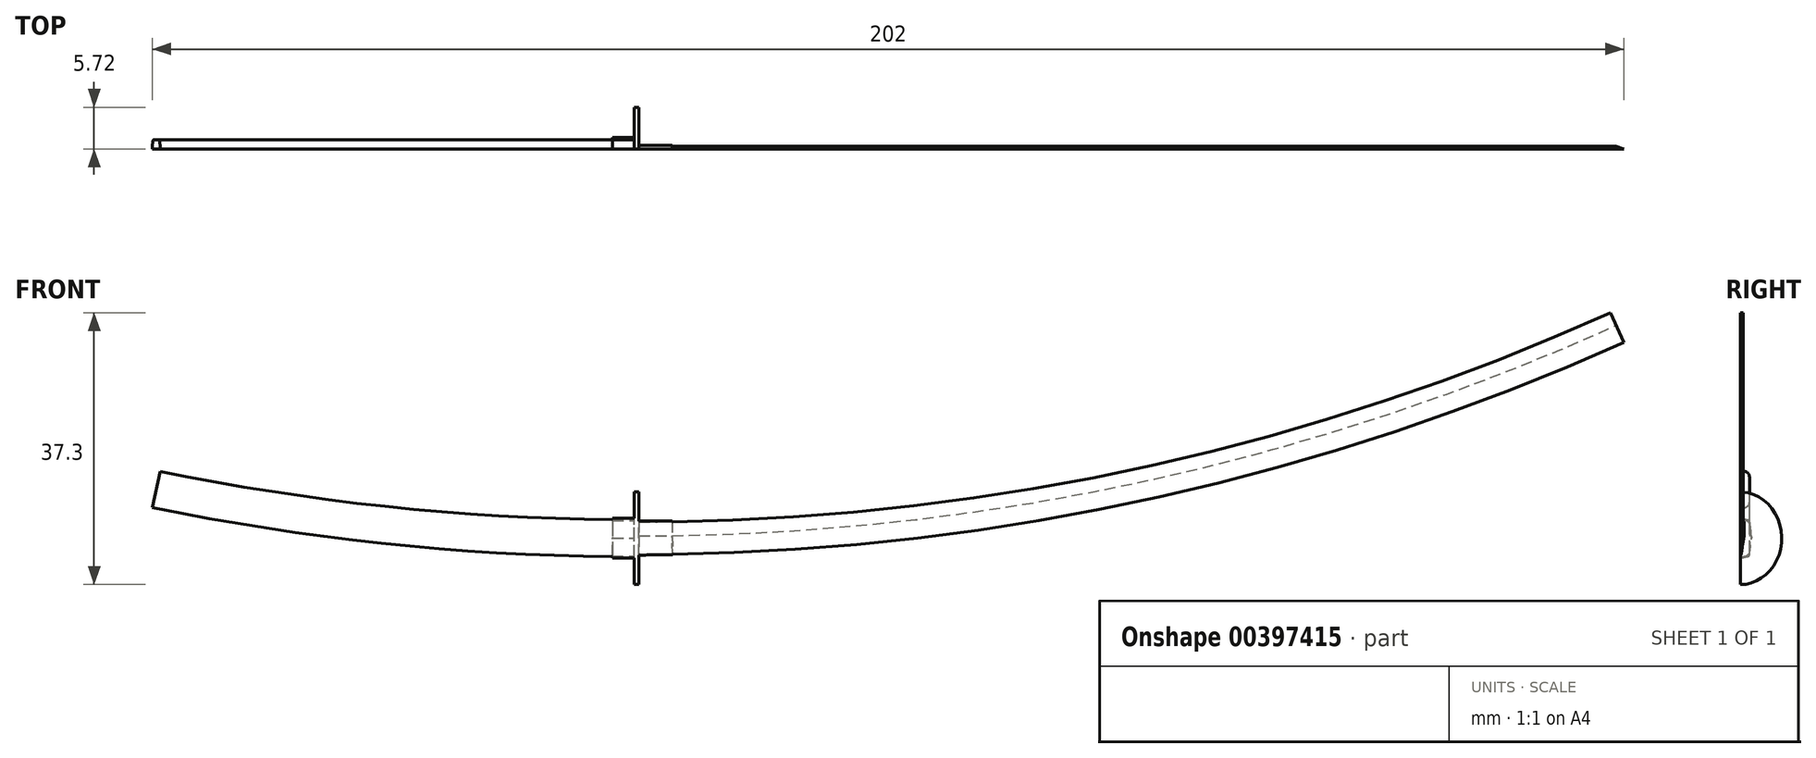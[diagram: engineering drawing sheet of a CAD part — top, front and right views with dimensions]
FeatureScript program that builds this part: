
annotation { "Feature Type Name" : "Feature", "Feature Type Description" : "" }
export const myFeature = defineFeature(function(context is Context, id is Id, definition is map)
    precondition{}
    {
        {
            var Q0;
            Q0=qCreatedBy(makeId("Front.planeOp"),FACE);
            var sketch = newSketch(context, id + "F0", { "sketchPlane" : qUnion([Q0])});
            skArc(sketch, "E0", {"start": v(0, 0) * mm, "mid": v(68.78, 7.3) * mm, "end": v(134.49, 28.9) * mm});
            skArc(sketch, "E1", {"start": v(0, 0) * mm, "mid": v(-33.12, 1.68) * mm, "end": v(-65.9, 6.7) * mm});
            skSolve(sketch);
        }
        {
            var Q0;
            Q0=qCreatedBy(makeId("Right.planeOp"),FACE);
            var sketch = newSketch(context, id + "F1", { "sketchPlane" : qUnion([Q0])});
            skLineSegment(sketch, "E2", {"start": v(0, 0) * mm, "end": v(0, 1.9) * mm});
            skLineSegment(sketch, "E3", {"start": v(0, 1.9) * mm, "end": v(0.38, 1.9) * mm});
            skLineSegment(sketch, "E4", {"start": v(0.38, 1.9) * mm, "end": v(0.38, 0) * mm});
            skLineSegment(sketch, "E5", {"start": v(0, 0) * mm, "end": v(0, -2.54) * mm});
            skLineSegment(sketch, "E6", {"start": v(0, -2.54) * mm, "end": v(0.38, 0) * mm});
            skSolve(sketch);
        }
        {
            var Q0;
            Q0=makeQuery(id+"F1.imprint","IMPRINT",FACE,{"disambiguationData":[TD([[makeQuery(id+"F1.imprint","IMPRINT",EDGE,{"derivedFrom":sQuery(id+"F1.wireOp",EDGE,"E2")}),-1.0]])]});
            var Q1;
            Q1=sQuery(id+"F0.wireOp",EDGE,"E0");
            sweep(context, id + "F2", {"profiles" : qUnion([Q0]), "path" : qUnion([Q1])});
        }
        {
            var Q0;
            Q0=qCreatedBy(makeId("Right.planeOp"),FACE);
            var sketch = newSketch(context, id + "F3", { "sketchPlane" : qUnion([Q0])});
            skLineSegment(sketch, "E7", {"start": v(0, 0) * mm, "end": v(0, 2.03) * mm});
            skLineSegment(sketch, "E8", {"start": v(0.5, 1.95) * mm, "end": v(0.5, 0) * mm});
            skLineSegment(sketch, "E9", {"start": v(0, 0) * mm, "end": v(0, -2.61) * mm});
            skLineSegment(sketch, "E10", {"start": v(0.5, 0) * mm, "end": v(0.12, -2.57) * mm});
            skLineSegment(sketch, "E11", {"start": v(0, 2.03) * mm, "end": v(0.5, 1.95) * mm});
            skLineSegment(sketch, "E12", {"start": v(0.12, -2.57) * mm, "end": v(0, -2.61) * mm});
            skSolve(sketch);
        }
        {
            var Q0;
            Q0=qCreatedBy(makeId("Front.planeOp"),FACE);
            var sketch = newSketch(context, id + "F4", { "sketchPlane" : qUnion([Q0])});
            skLineSegment(sketch, "E13", {"start": v(0, 0) * mm, "end": v(0, 327.47) * mm});
            skArc(sketch, "E14", {"start": v(0, 0) * mm, "mid": v(2.45, 0) * mm, "end": v(4.9, 0.04) * mm});
            skSolve(sketch);
        }
        {
            var Q0;
            Q0=makeQuery(id+"F3.imprint","IMPRINT",FACE,{"disambiguationData":[TD([[makeQuery(id+"F3.imprint","IMPRINT",EDGE,{"derivedFrom":sQuery(id+"F3.wireOp",EDGE,"E7")}),-1.0]])]});
            var Q1;
            Q1=sQuery(id+"F4.wireOp",EDGE,"E14");
            sweep(context, id + "F5", {"operationType" : NewBodyOperationType.ADD, "profiles" : qUnion([Q0]), "path" : qUnion([Q1])});
        }
        {
            var Q0;
            Q0=qCreatedBy(makeId("Right.planeOp"),FACE);
            var sketch = newSketch(context, id + "F6", { "sketchPlane" : qUnion([Q0])});
            skLineSegment(sketch, "E15", {"start": v(0, 0) * mm, "end": v(0, -0.32) * mm});
            skEllipticalArc(sketch, "E16", {});
            skLineSegment(sketch, "E17", {"start": v(0, 6.03) * mm, "end": v(0, -6.67) * mm});
            skFitSpline(sketch, "E18.0", {"points": [v(-0.74, -4.84) * mm, v(0, -4.92) * mm, v(0.74, -4.84) * mm, v(1.45, -4.6) * mm, v(2.13, -4.2) * mm, v(2.74, -3.64) * mm, v(3.25, -2.95) * mm, v(3.64, -2.14) * mm, v(3.88, -1.25) * mm, v(3.96, -0.32) * mm, v(3.88, 0.62) * mm, v(3.64, 1.5) * mm, v(3.25, 2.32) * mm, v(2.74, 3) * mm, v(2.13, 3.56) * mm, v(1.45, 3.96) * mm, v(0.74, 4.2) * mm, v(0, 4.28) * mm, v(-0.74, 4.2) * mm, v(-1.45, 3.96) * mm, v(-2.13, 3.56) * mm, v(-2.74, 3) * mm, v(-3.25, 2.32) * mm, v(-3.64, 1.5) * mm, v(-3.88, 0.62) * mm, v(-3.96, -0.32) * mm, v(-3.88, -1.25) * mm, v(-3.64, -2.14) * mm, v(-3.25, -2.95) * mm, v(-2.74, -3.64) * mm, v(-2.13, -4.2) * mm, v(-1.45, -4.6) * mm, v(-0.74, -4.84) * mm, v(0, -4.92) * mm, v(0.74, -4.84) * mm]});
            skLineSegment(sketch, "E18.1", {"start": v(1.78, 3.76) * mm, "end": v(1.78, -4.4) * mm});
            const initialGuessF6  = {"E16": [0, -0.0003175000000000001, 0, -1, 0.00635, 0.005715, 0, 3.141592653589793]};
            skSetInitialGuess(sketch, initialGuessF6);
            skSolve(sketch);
        }
        {
            var Q0;
            {var subQ0=sQuery(id+"F6.wireOp",EDGE,"E16");Q0=makeQuery(id+"F6.imprint","IMPRINT",FACE,{"disambiguationData":[TD([[makeQuery(id+"F6.imprint","IMPRINT",EDGE,{"derivedFrom":subQ0}),1.0]])]});}
            extrude(context, id + "F7", {"entities" : qUnion([Q0]), "operationType" : NewBodyOperationType.ADD, "endBound" : BoundingType.SYMMETRIC, "depth" : 0.64 * mm});
        }
        {
            var Q0;
            Q0=qCreatedBy(makeId("Right.planeOp"),FACE);
            var sketch = newSketch(context, id + "F8", { "sketchPlane" : qUnion([Q0])});
            skLineSegment(sketch, "E19", {"start": v(0, 0) * mm, "end": v(0, -0.32) * mm});
            skLineSegment(sketch, "E20.bottom", {"start": v(0.5, -2.86) * mm, "end": v(0, -2.86) * mm});
            skLineSegment(sketch, "E20.top", {"start": v(0.5, 2.22) * mm, "end": v(0, 2.22) * mm});
            skLineSegment(sketch, "E20.left", {"start": v(1.27, -2.1) * mm, "end": v(1.27, 1.46) * mm});
            skPoint(sketch, "E20.middle", {"position": v(0, -0.32) * mm});
            skLineSegment(sketch, "E21", {"start": v(0, 2.22) * mm, "end": v(0, -2.86) * mm});
            skPoint(sketch, "E20.right.start.orphan", {"position": v(-1.27, -2.86) * mm});
            skPoint(sketch, "E22.orphan", {"position": v(-1.27, 2.22) * mm});
            skPoint(sketch, "E23.visualSharp", {"position": v(1.27, 2.22) * mm});
            skArc(sketch, "E23.filletArc", {"start": v(1.27, 1.46) * mm, "mid": v(1.05, 2) * mm, "end": v(0.5, 2.22) * mm});
            skPoint(sketch, "E24.visualSharp", {"position": v(1.27, -2.86) * mm});
            skArc(sketch, "E24.filletArc", {"start": v(0.5, -2.86) * mm, "mid": v(1.05, -2.63) * mm, "end": v(1.27, -2.1) * mm});
            skSolve(sketch);
        }
        {
            var Q0;
            Q0 = qSketchRegion(id + "F8", true);
            var Q1;
            Q1=sQuery(id+"F0.wireOp",EDGE,"E1");
            sweep(context, id + "F9", {"operationType" : NewBodyOperationType.ADD, "profiles" : qUnion([Q0]), "path" : qUnion([Q1])});
        }
        {
            var Q0;
            Q0=qCreatedBy(makeId("Right.planeOp"),FACE);
            var sketch = newSketch(context, id + "F10", { "sketchPlane" : qUnion([Q0])});
            skLineSegment(sketch, "E25", {"start": v(0, 0) * mm, "end": v(0, -3.05) * mm});
            skLineSegment(sketch, "E26", {"start": v(0, -3.05) * mm, "end": v(1.24, -2.76) * mm});
            skLineSegment(sketch, "E27", {"start": v(1.24, -2.76) * mm, "end": v(1.58, -0.32) * mm});
            skLineSegment(sketch, "E28.MirrorCS", {"start": v(1.24, 2.13) * mm, "end": v(1.58, -0.32) * mm});
            skLineSegment(sketch, "E29.MirrorCS", {"start": v(0, 2.41) * mm, "end": v(1.24, 2.13) * mm});
            skLineSegment(sketch, "E30", {"start": v(0, 2.41) * mm, "end": v(0, -3.05) * mm});
            skSolve(sketch);
        }
        {
            var Q0;
            Q0=qCreatedBy(makeId("Front.planeOp"),FACE);
            var sketch = newSketch(context, id + "F11", { "sketchPlane" : qUnion([Q0])});
            skArc(sketch, "E31", {"start": v(0, 0) * mm, "mid": v(-1.65, 0) * mm, "end": v(-3.3, 0.02) * mm});
            skSolve(sketch);
        }
        {
            var Q0;
            Q0 = qSketchRegion(id + "F10", true);
            var Q1;
            Q1 = qConstructionFilter(qBodyType(qCreatedBy(id + "F11" ,EDGE), BodyType.WIRE), ConstructionObject.NO);
            sweep(context, id + "F12", {"operationType" : NewBodyOperationType.ADD, "profiles" : qUnion([Q0]), "path" : qUnion([Q1])});
        }
    });
